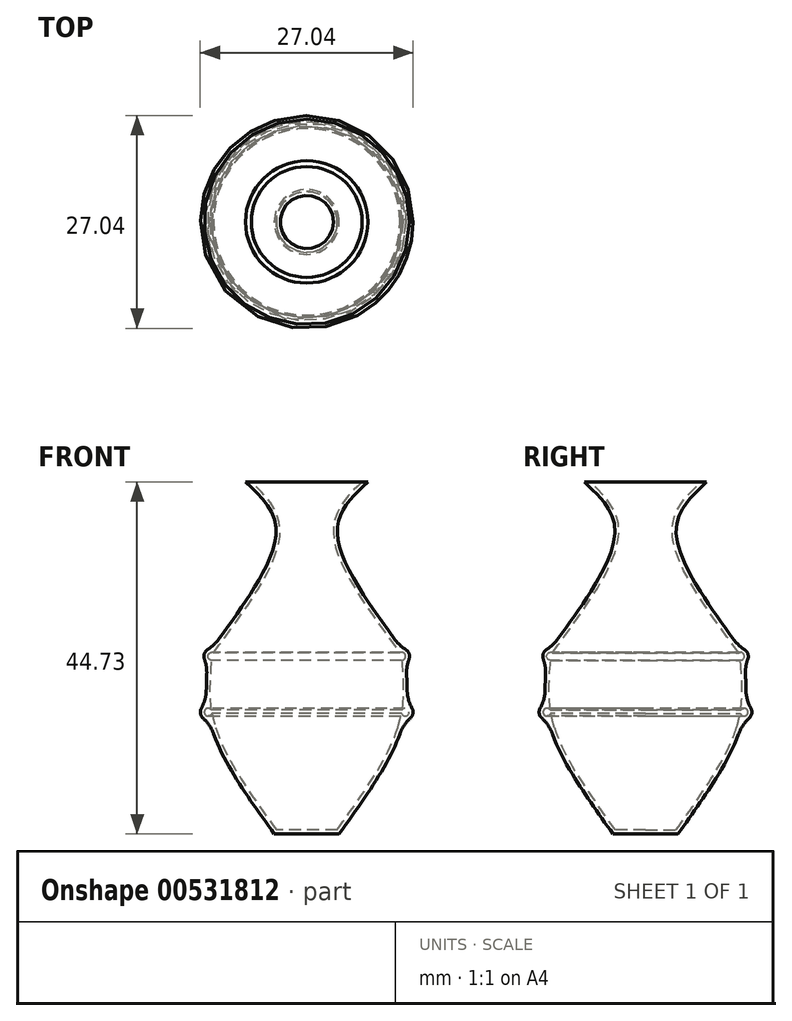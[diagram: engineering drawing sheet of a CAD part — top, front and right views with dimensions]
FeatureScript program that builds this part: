
annotation { "Feature Type Name" : "Feature", "Feature Type Description" : "" }
export const myFeature = defineFeature(function(context is Context, id is Id, definition is map)
    precondition{}
    {
        {
            var Q0;
            Q0=qCreatedBy(makeId("Front.planeOp"),FACE);
            var sketch = newSketch(context, id + "F0", { "sketchPlane" : qUnion([Q0])});
            skLineSegment(sketch, "E0", {"start": v(0, 31.34) * mm, "end": v(-7.77, 31.34) * mm});
            skLineSegment(sketch, "E1", {"start": v(-12.06, 0) * mm, "end": v(0, 0) * mm});
            skLineSegment(sketch, "E2", {"start": v(0, 31.34) * mm, "end": v(0, 0) * mm});
            skLineSegment(sketch, "E3", {"start": v(0, 0) * mm, "end": v(0, -13.4) * mm});
            skLineSegment(sketch, "E4", {"start": v(0, -13.4) * mm, "end": v(-4.12, -13.4) * mm});
            skPoint(sketch, "E5.1.internal.snap0", {"position": v(0, -6.7) * mm});
            skLineSegment(sketch, "E6", {"start": v(-12.06, 10.18) * mm, "end": v(-9.46, 10.18) * mm});
            skLineSegment(sketch, "E7", {"start": v(-9.46, 10.18) * mm, "end": v(-9.46, 8.34) * mm});
            skLineSegment(sketch, "E8", {"start": v(-9.46, 8.34) * mm, "end": v(-12.6, 8.34) * mm});
            skPoint(sketch, "E9.1.internal.snap0", {"position": v(-3.88, 31.34) * mm});
            skFitSpline(sketch, "E9", {"points": [v(-7.77, 31.34) * mm, v(-3.88, 25.3) * mm, v(-12.06, 10.18) * mm], "startDerivative": vector(14.48, -13.53) * mm, "endDerivative": vector(-20.54, -27.78) * mm});
            skFitSpline(sketch, "E10", {"points": [v(-12.6, 8.34) * mm, v(-12.06, 0) * mm, v(-4.12, -13.4) * mm], "startDerivative": vector(-1.36, -18.98) * mm, "endDerivative": vector(17.35, -24.21) * mm});
            skFitSpline(sketch, "E11", {"points": [v(-12.06, 10.18) * mm, v(-12.6, 8.34) * mm], "startDerivative": vector(-0.54, -1.84) * mm, "endDerivative": vector(-0.54, -1.84) * mm});
            skArc(sketch, "E12", {"start": v(-12.06, 10.18) * mm, "mid": v(-13.02, 9.46) * mm, "end": v(-12.6, 8.34) * mm});
            skArc(sketch, "E13", {"start": v(-12.67, 3.07) * mm, "mid": v(-13.5, 1.92) * mm, "end": v(-12.35, 1.1) * mm});
            skSolve(sketch);
        }
        {
            var Q0;
            Q0 = qSketchRegion(id + "F0", true);
            var Q1;
            Q1=sQuery(id+"F0.wireOp",EDGE,"E2");
            revolve(context, id + "F1", {"entities" : qUnion([Q0]), "axis" : qUnion([Q1]), "revolveType" : RevolveType.FULL});
        }
        {
            var Q0;
            Q0=makeQuery(id+"F1.opRevolve","SWEPT_FACE",FACE,{"disambiguationData":[OSD([sQuery(id+"F0.wireOp",EDGE,"E0")])]});
            shell(context, id + "F2", {"entities" : qUnion([Q0]), "thickness" : 0.5 * mm});
        }
        {
            var Q0;
            Q0=makeQuery(id+"F1.opRevolve","SWEPT_EDGE",EDGE,{"disambiguationData":[OSD([sQuery(id+"F0.wireOp",EDGE,"E6"),sQuery(id+"F0.wireOp",EDGE,"E9"),sQuery(id+"F0.wireOp",EDGE,"E11"),sQuery(id+"F0.wireOp",EDGE,"E12")])]});
            var Q1;
            {var subQ0=sQuery(id+"F0.wireOp",EDGE,"E13");var subQ1=sQuery(id+"F0.wireOp",EDGE,"E10");Q1=makeQuery(id+"F1.opRevolve","SWEPT_EDGE",EDGE,{"disambiguationData":[OSD([subQ1,subQ0]),TDD([makeQuery(id+"F0.imprint","INTERSECT",VERTEX,{"disambiguationData":[OD(1.0)],"derivedFrom":[subQ1,subQ0]})])]});}
            var Q2;
            {var subQ0=sQuery(id+"F0.wireOp",EDGE,"E13");var subQ1=sQuery(id+"F0.wireOp",EDGE,"E10");Q2=makeQuery(id+"F1.opRevolve","SWEPT_EDGE",EDGE,{"disambiguationData":[OSD([subQ1,subQ0]),TDD([makeQuery(id+"F0.imprint","INTERSECT",VERTEX,{"disambiguationData":[OD(0.0)],"derivedFrom":[subQ1,subQ0]})])]});}
            var Q3;
            Q3=makeQuery(id+"F1.opRevolve","SWEPT_EDGE",EDGE,{"disambiguationData":[OSD([sQuery(id+"F0.wireOp",EDGE,"E8"),sQuery(id+"F0.wireOp",EDGE,"E10"),sQuery(id+"F0.wireOp",EDGE,"E11"),sQuery(id+"F0.wireOp",EDGE,"E12")])]});
            fillet(context, id + "F3", {"entities" : qUnion([Q0, Q1, Q2, Q3]), "radius" : 5 * mm, "tangentPropagation" : true, "allowEdgeOverflow" : false});
        }
    });
